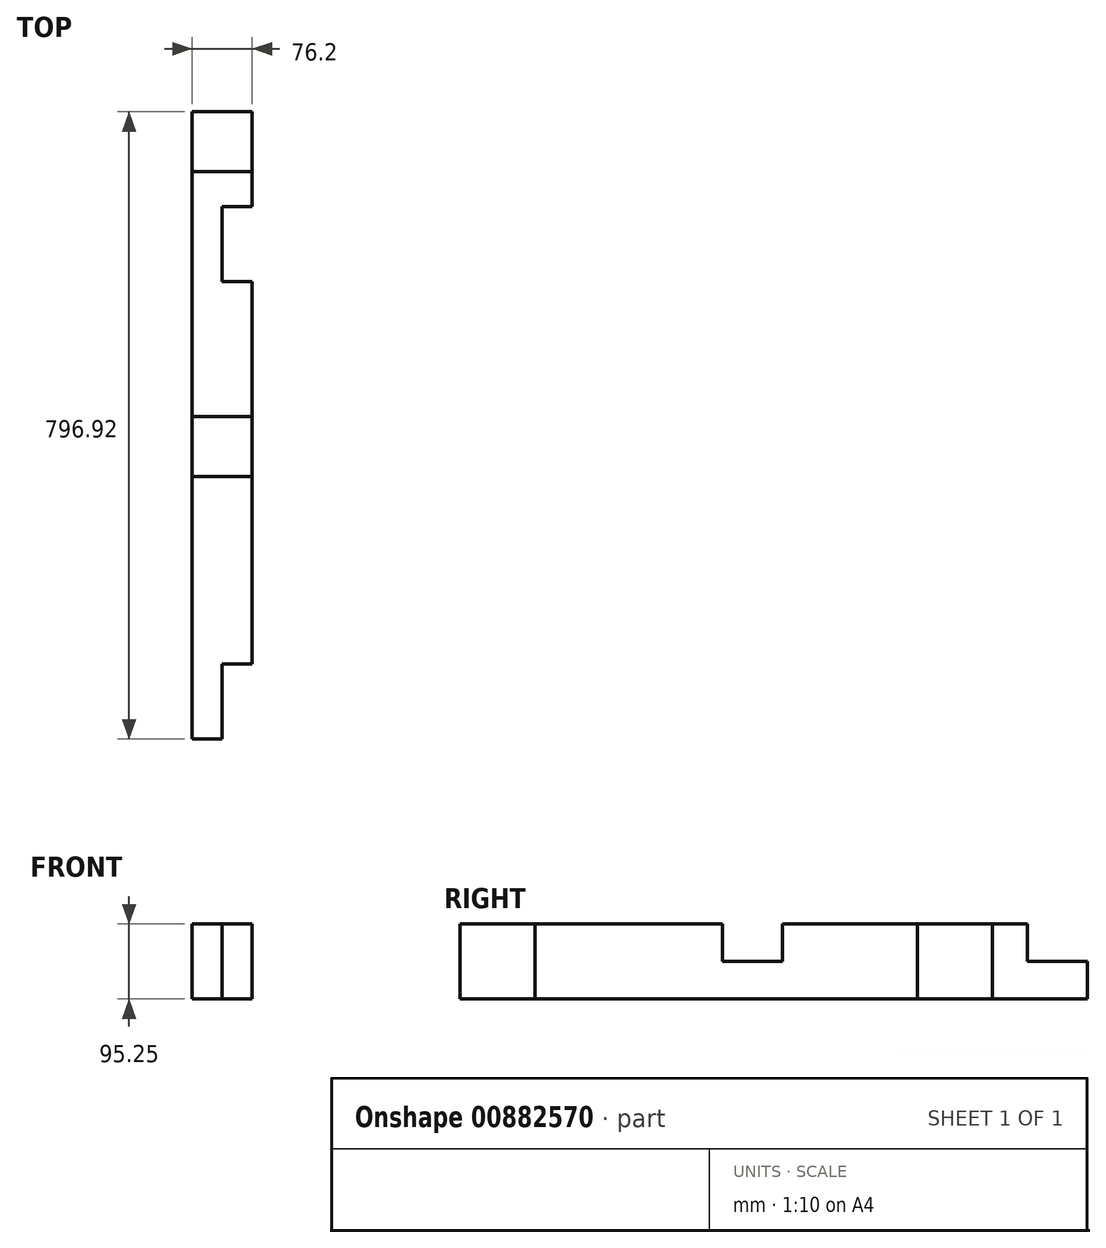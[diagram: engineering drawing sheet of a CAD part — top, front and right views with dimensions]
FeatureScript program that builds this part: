
annotation { "Feature Type Name" : "Feature", "Feature Type Description" : "" }
export const myFeature = defineFeature(function(context is Context, id is Id, definition is map)
    precondition{}
    {
        {
            var Q0;
            Q0=qCreatedBy(makeId("Front.planeOp"),FACE);
            var sketch = newSketch(context, id + "F0", { "sketchPlane" : qUnion([Q0])});
            skLineSegment(sketch, "E0.bottom", {"start": v(0, 0) * mm, "end": v(76.2, 0) * mm});
            skLineSegment(sketch, "E0.top", {"start": v(0, 95.25) * mm, "end": v(76.2, 95.25) * mm});
            skLineSegment(sketch, "E0.left", {"start": v(0, 0) * mm, "end": v(0, 95.25) * mm});
            skLineSegment(sketch, "E0.right", {"start": v(76.2, 0) * mm, "end": v(76.2, 95.25) * mm});
            skSolve(sketch);
        }
        {
            var Q0;
            Q0=qSketchRegion(id+"F0",true);
            extrude(context, id + "F1", {"entities" : qUnion([Q0]), "depth" : 796.92 * mm, "offsetDistance" : 25.4 * mm});
        }
        {
            var Q0;
            Q0=makeQuery(id+"F1.opExtrude","SWEPT_FACE",FACE,{"disambiguationData":[OSD([sQuery(id+"F0.wireOp",EDGE,"E0.right")])]});
            var sketch = newSketch(context, id + "F2", { "sketchPlane" : qUnion([Q0])});
            skLineSegment(sketch, "E1.bottom", {"start": v(-796.93, 95.25) * mm, "end": v(-701.68, 95.25) * mm});
            skLineSegment(sketch, "E1.top", {"start": v(-796.93, 0) * mm, "end": v(-701.68, 0) * mm});
            skLineSegment(sketch, "E1.left", {"start": v(-796.93, 95.25) * mm, "end": v(-796.93, 0) * mm});
            skLineSegment(sketch, "E1.right", {"start": v(-701.68, 95.25) * mm, "end": v(-701.68, 0) * mm});
            skSolve(sketch);
        }
        {
            var Q0;
            Q0 = qSketchRegion(id + "F2", true);
            extrude(context, id + "F3", {"entities" : qUnion([Q0]), "operationType" : NewBodyOperationType.REMOVE, "oppositeDirection" : true, "depth" : 38.1 * mm, "offsetDistance" : 25.4 * mm});
        }
        {
            var Q0;
            Q0=makeQuery(id+"F1.opExtrude","SWEPT_FACE",FACE,{"disambiguationData":[OSD([sQuery(id+"F0.wireOp",EDGE,"E0.right")])]});
            var sketch = newSketch(context, id + "F4", { "sketchPlane" : qUnion([Q0])});
            skLineSegment(sketch, "E2.bottom", {"start": v(-463.55, 95.25) * mm, "end": v(-387.35, 95.25) * mm});
            skLineSegment(sketch, "E2.top", {"start": v(-463.55, 47.62) * mm, "end": v(-387.35, 47.62) * mm});
            skLineSegment(sketch, "E2.left", {"start": v(-463.55, 95.25) * mm, "end": v(-463.55, 47.63) * mm});
            skLineSegment(sketch, "E2.right", {"start": v(-387.35, 95.25) * mm, "end": v(-387.35, 47.63) * mm});
            skLineSegment(sketch, "E3.bottom", {"start": v(-76.2, 95.25) * mm, "end": v(0, 95.25) * mm});
            skLineSegment(sketch, "E3.top", {"start": v(-76.2, 47.62) * mm, "end": v(0, 47.62) * mm});
            skLineSegment(sketch, "E3.left", {"start": v(-76.2, 95.25) * mm, "end": v(-76.2, 47.62) * mm});
            skLineSegment(sketch, "E3.right", {"start": v(0, 95.25) * mm, "end": v(0, 47.62) * mm});
            skSolve(sketch);
        }
        {
            var Q0;
            Q0 = qSketchRegion(id + "F4", true);
            extrude(context, id + "F5", {"entities" : qUnion([Q0]), "operationType" : NewBodyOperationType.REMOVE, "endBound" : BoundingType.THROUGH_ALL, "oppositeDirection" : true, "depth" : 25.4 * mm, "offsetDistance" : 25.4 * mm});
        }
        {
            var Q0;
            Q0=makeQuery(id+"F1.opExtrude","SWEPT_FACE",FACE,{"disambiguationData":[OSD([sQuery(id+"F0.wireOp",EDGE,"E0.right")])]});
            var sketch = newSketch(context, id + "F6", { "sketchPlane" : qUnion([Q0])});
            skLineSegment(sketch, "E4.bottom", {"start": v(-120.65, 95.25) * mm, "end": v(-215.9, 95.25) * mm});
            skLineSegment(sketch, "E4.top", {"start": v(-120.65, 0) * mm, "end": v(-215.9, 0) * mm});
            skLineSegment(sketch, "E4.left", {"start": v(-120.65, 95.25) * mm, "end": v(-120.65, 0) * mm});
            skLineSegment(sketch, "E4.right", {"start": v(-215.9, 95.25) * mm, "end": v(-215.9, 0) * mm});
            skSolve(sketch);
        }
        {
            var Q0;
            Q0 = qSketchRegion(id + "F6", true);
            extrude(context, id + "F7", {"entities" : qUnion([Q0]), "operationType" : NewBodyOperationType.REMOVE, "oppositeDirection" : true, "depth" : 38.1 * mm, "offsetDistance" : 25.4 * mm});
        }
    });
